# Revit family: LHBN48
name_source: partatom
category: Lighting Fixtures
units: mm (PartAtom-declared; Revit-internal decimal feet)

## family parameters
Always vertical = Yes
Cut with Voids When Loaded = No
Host = Ceiling
Light Source = Yes
Maintain Annotation Orientation = No
OmniClass Number = 23.80.70.11.14.11
OmniClass Title = Downlights
Part Type = Normal
Room Calculation Point = No
Round Connector Dimension = Use Diameter
Shared = No

## types (8) — shared parameters
Assembly Code = D5020200
Color Filter = 16777215
Default Elevation = 0' - 0"
Description = LED - Linear High-Bay Narrow
Dimming Lamp Color Temperature Shift = <None>
Emit Shape Visible in Rendering = No
Emit from Rectangle Length = 3' - 11 3/4"
Emit from Rectangle Width = 1' - 4"
Height = 0' - 5 1/2"
Housing Finish = Metal - Viscor - White
Lamp = LED
Length = 3' - 11 3/4"
Lens Finish = Acrylic - Viscor - Frosted, Impact Round Extruded
Louver Finish = Metal - Viscor - White Gloss F06
Manufacturer = VISIONEERING by VISCOR
Model = LHBN
Tilt Angle = 90.00°
URL = https://viscor.com
Voltage = 120 V
Width = 1' - 4"

## per-type parameters (varying)
| type | Apparent Load | Lamp Wattage | Photometric Web File |
| LHBN48-LED840K120LUNV-C27 | 100 VA | 100 VA | LHBN48-LED840K120LUNV-C27.ies |
| LHBN48-LED840K150LUNV-C27 | 118 VA | 118 VA | LHBN48-LED840K150LUNV-C27.ies |
| LHBN48-LED840K180LUNV-C27 | 159 VA | 159 VA | LHBN48-LED840K180LUNV-C27.ies |
| LHBN48-LED840K240LUNV-C27 | 205 VA | 205 VA | LHBN48-LED840K240LUNV-C27.ies |
| LHBN48-LED840K120LUNV | 100 VA | 100 VA | LHBN48-LED840K120LUNV.ies |
| LHBN48-LED840K150LUNV | 118 VA | 118 VA | LHBN48-LED840K150LUNV.ies |
| LHBN48-LED840K180LUNV | 159 VA | 159 VA | LHBN48-LED840K180LUNV.ies |
| LHBN48-LED840K240LUNV | 205 VA | 205 VA | LHBN48-LED840K240LUNV.ies |

## geometry (parser evidence)
native form markers: Sweep x3
no freeform markers — native parametric forms only
